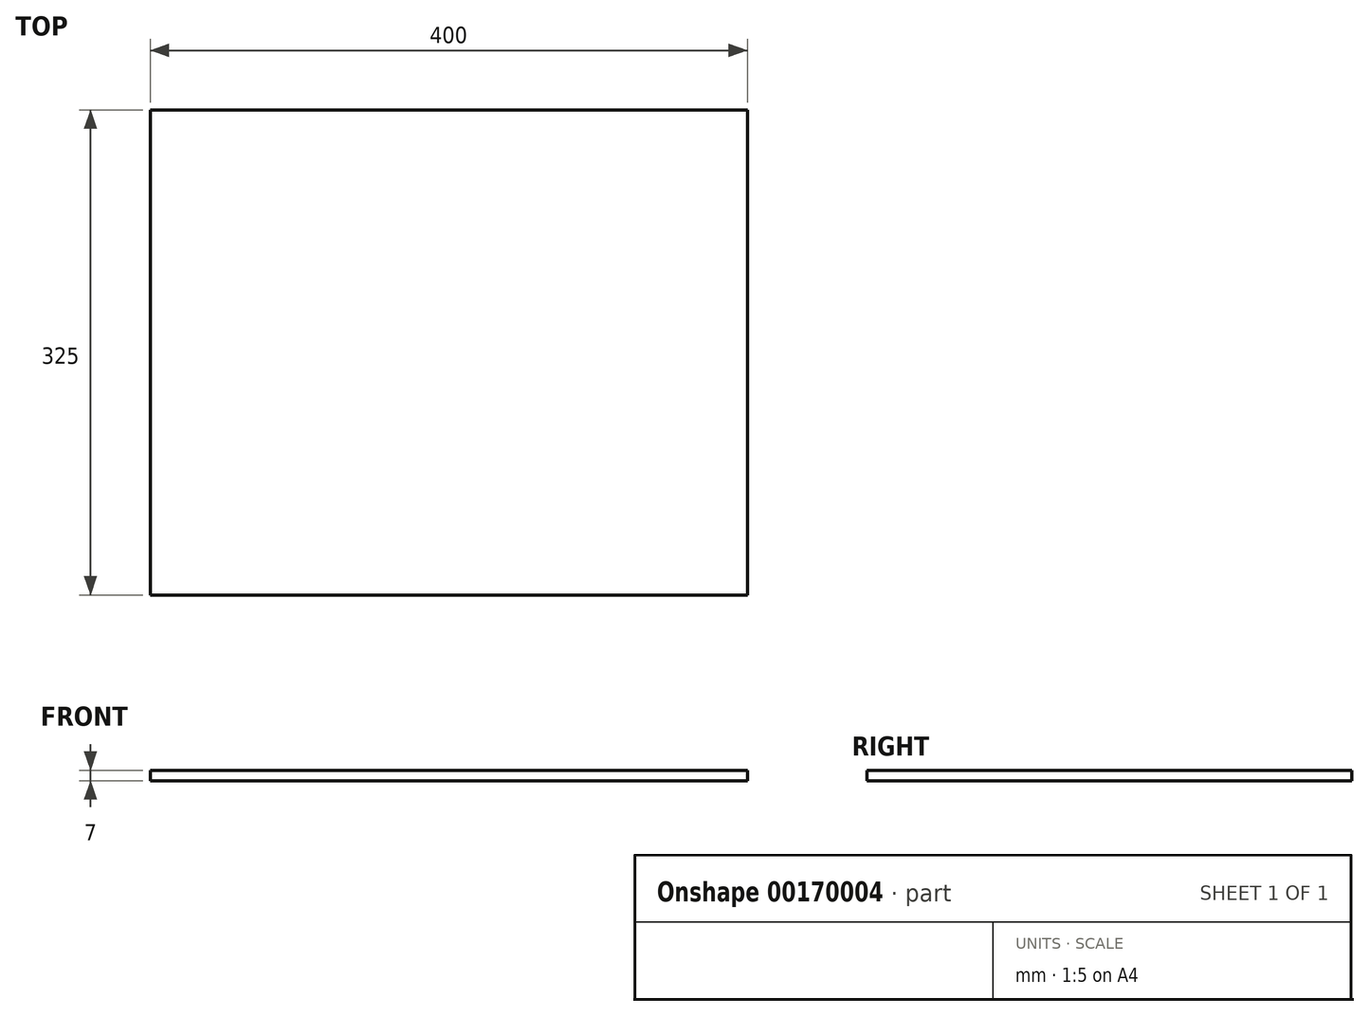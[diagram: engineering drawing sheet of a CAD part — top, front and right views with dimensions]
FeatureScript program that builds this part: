
annotation { "Feature Type Name" : "Feature", "Feature Type Description" : "" }
export const myFeature = defineFeature(function(context is Context, id is Id, definition is map)
    precondition{}
    {
        {
            var Q0;
            Q0=qCreatedBy(makeId("Top.planeOp"),FACE);
            var sketch = newSketch(context, id + "F0", { "sketchPlane" : qUnion([Q0])});
            skLineSegment(sketch, "E0.bottom", {"start": v(200, -162.5) * mm, "end": v(-200, -162.5) * mm});
            skLineSegment(sketch, "E0.top", {"start": v(200, 162.5) * mm, "end": v(-200, 162.5) * mm});
            skLineSegment(sketch, "E0.left", {"start": v(200, -162.5) * mm, "end": v(200, 162.5) * mm});
            skLineSegment(sketch, "E0.right", {"start": v(-200, -162.5) * mm, "end": v(-200, 162.5) * mm});
            skPoint(sketch, "E0.middle", {"position": v(0, 0) * mm});
            skSolve(sketch);
        }
        {
            var Q0;
            Q0=makeQuery(id+"F0.imprint","IMPRINT",FACE,{"disambiguationData":[TD([[makeQuery(id+"F0.imprint","IMPRINT",EDGE,{"derivedFrom":sQuery(id+"F0.wireOp",EDGE,"E0.bottom")}),-1.0]])]});
            extrude(context, id + "F1", {"entities" : qUnion([Q0]), "depth" : 7 * mm});
        }
    });
